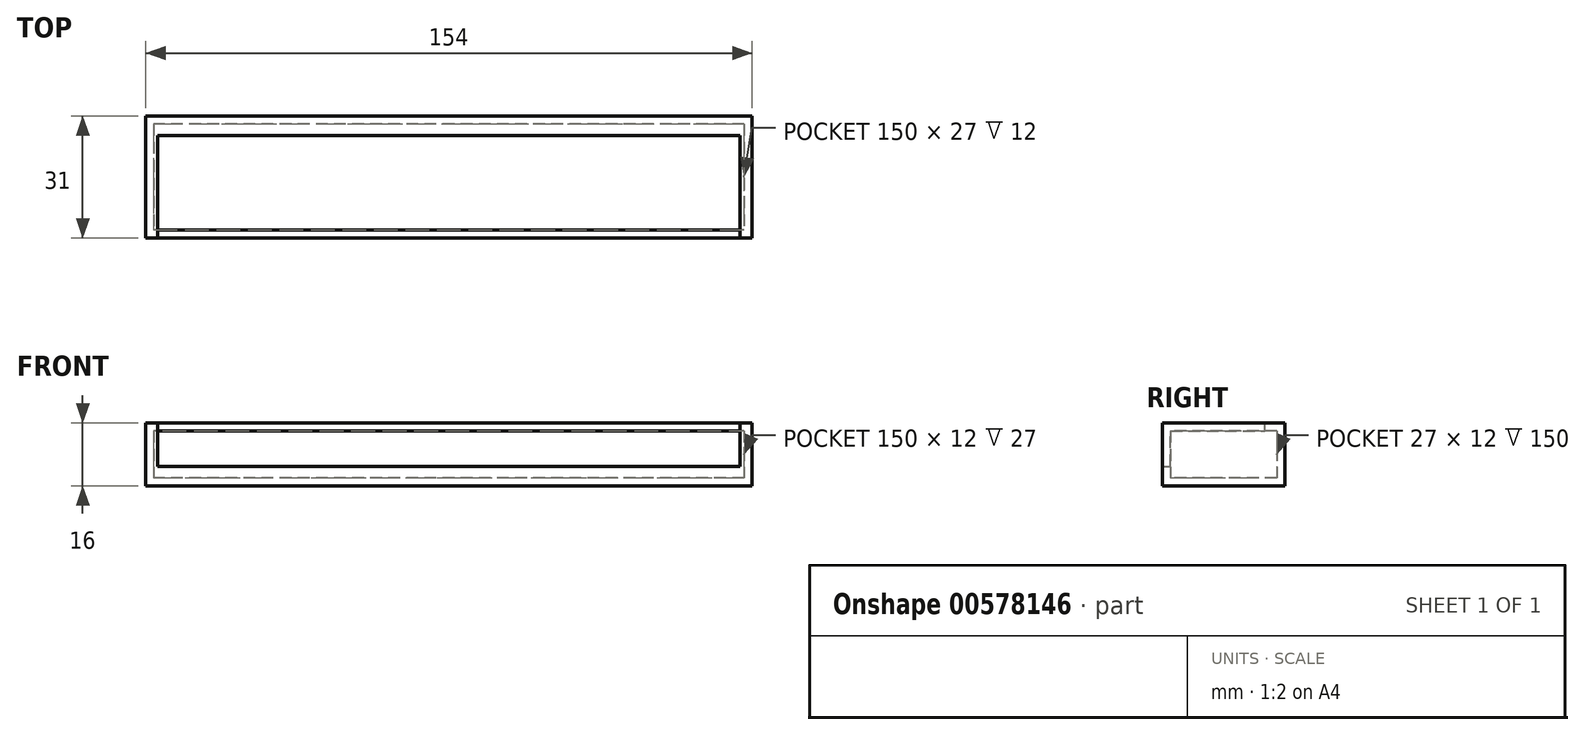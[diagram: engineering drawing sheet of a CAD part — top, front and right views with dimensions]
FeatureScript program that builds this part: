
annotation { "Feature Type Name" : "Feature", "Feature Type Description" : "" }
export const myFeature = defineFeature(function(context is Context, id is Id, definition is map)
    precondition{}
    {
        {
            var Q0;
            Q0=qCreatedBy(makeId("Top.planeOp"),FACE);
            var sketch = newSketch(context, id + "F0", { "sketchPlane" : qUnion([Q0])});
            skLineSegment(sketch, "E0.bottom", {"start": v(77, 15.5) * mm, "end": v(-77, 15.5) * mm});
            skLineSegment(sketch, "E0.top", {"start": v(77, -15.5) * mm, "end": v(-77, -15.5) * mm});
            skLineSegment(sketch, "E0.left", {"start": v(77, 15.5) * mm, "end": v(77, -15.5) * mm});
            skLineSegment(sketch, "E0.right", {"start": v(-77, 15.5) * mm, "end": v(-77, -15.5) * mm});
            skPoint(sketch, "E0.middle", {"position": v(0, 0) * mm});
            skSolve(sketch);
        }
        {
            var Q0;
            Q0=makeQuery(id+"F0.imprint","IMPRINT",FACE,{"disambiguationData":[TD([[makeQuery(id+"F0.imprint","IMPRINT",EDGE,{"derivedFrom":sQuery(id+"F0.wireOp",EDGE,"E0.bottom")}),1.0]])]});
            extrude(context, id + "F1", {"entities" : qUnion([Q0]), "endBound" : BoundingType.SYMMETRIC, "depth" : 16 * mm, "offsetDistance" : 25 * mm});
        }
        {
            var Q0;
            Q0=qCreatedBy(makeId("Top.planeOp"),FACE);
            var sketch = newSketch(context, id + "F2", { "sketchPlane" : qUnion([Q0])});
            skLineSegment(sketch, "E1.bottom", {"start": v(75, 13.5) * mm, "end": v(-75, 13.5) * mm});
            skLineSegment(sketch, "E1.top", {"start": v(75, -13.5) * mm, "end": v(-75, -13.5) * mm});
            skLineSegment(sketch, "E1.left", {"start": v(75, 13.5) * mm, "end": v(75, -13.5) * mm});
            skLineSegment(sketch, "E1.right", {"start": v(-75, 13.5) * mm, "end": v(-75, -13.5) * mm});
            skPoint(sketch, "E1.middle", {"position": v(0, 0) * mm});
            skSolve(sketch);
        }
        {
            var Q0;
            Q0 = qSketchRegion(id + "F2", true);
            extrude(context, id + "F3", {"entities" : qUnion([Q0]), "operationType" : NewBodyOperationType.REMOVE, "endBound" : BoundingType.SYMMETRIC, "depth" : 12 * mm, "offsetDistance" : 25 * mm});
        }
        {
            var Q0;
            Q0=makeQuery(id+"F1.opExtrude","CAP_FACE",FACE,{"disambiguationData":[OSD([sQuery(id+"F0.wireOp",EDGE,"E0.bottom"),sQuery(id+"F0.wireOp",EDGE,"E0.top"),sQuery(id+"F0.wireOp",EDGE,"E0.left"),sQuery(id+"F0.wireOp",EDGE,"E0.right")])],"isStart":false});
            var sketch = newSketch(context, id + "F4", { "sketchPlane" : qUnion([Q0])});
            skLineSegment(sketch, "E2.bottom", {"start": v(-74, -15.5) * mm, "end": v(74, -15.5) * mm});
            skLineSegment(sketch, "E2.top", {"start": v(-74, 10.5) * mm, "end": v(74, 10.5) * mm});
            skLineSegment(sketch, "E2.left", {"start": v(-74, -15.5) * mm, "end": v(-74, 10.5) * mm});
            skLineSegment(sketch, "E2.right", {"start": v(74, -15.5) * mm, "end": v(74, 10.5) * mm});
            skSolve(sketch);
        }
        {
            var Q0;
            Q0 = qSketchRegion(id + "F4", true);
            extrude(context, id + "F5", {"entities" : qUnion([Q0]), "operationType" : NewBodyOperationType.REMOVE, "oppositeDirection" : true, "depth" : 11 * mm, "offsetDistance" : 25 * mm});
        }
    });
